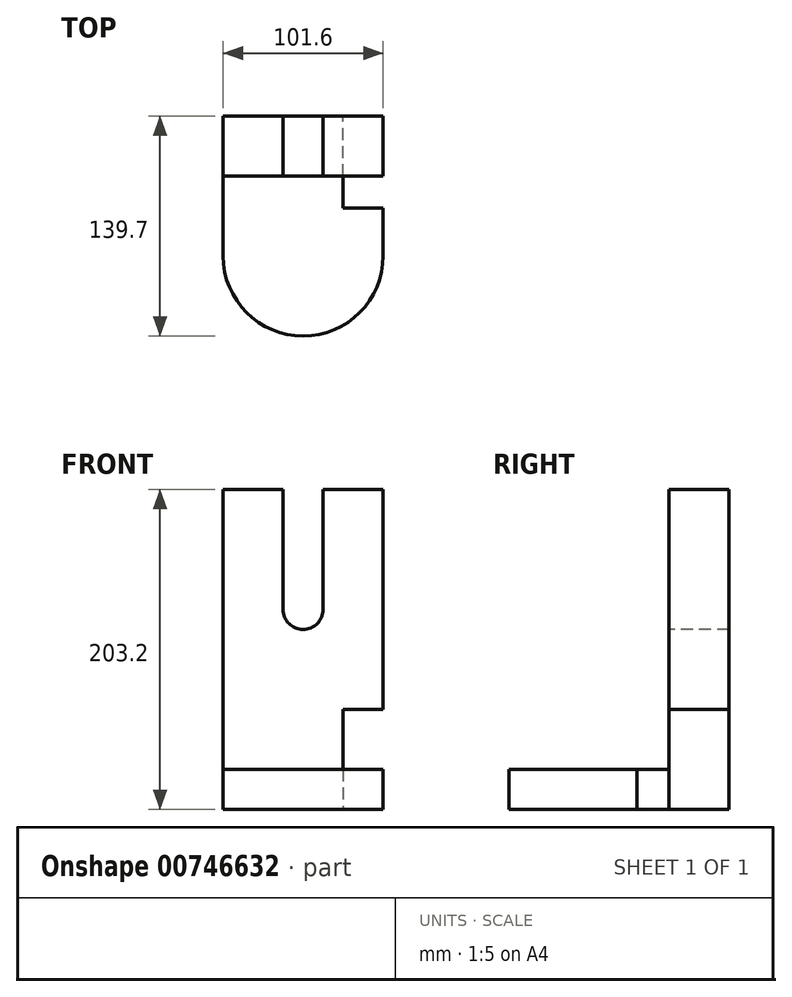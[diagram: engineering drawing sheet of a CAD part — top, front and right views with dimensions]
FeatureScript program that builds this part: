
annotation { "Feature Type Name" : "Feature", "Feature Type Description" : "" }
export const myFeature = defineFeature(function(context is Context, id is Id, definition is map)
    precondition{}
    {
        {
            var Q0;
            Q0=qCreatedBy(makeId("Front.planeOp"),FACE);
            var sketch = newSketch(context, id + "F0", { "sketchPlane" : qUnion([Q0])});
            skLineSegment(sketch, "E0.top", {"start": v(-50.8, -101.6) * mm, "end": v(50.8, -101.6) * mm});
            skLineSegment(sketch, "E0.left", {"start": v(-50.8, 101.6) * mm, "end": v(-50.8, -101.6) * mm});
            skLineSegment(sketch, "E0.right", {"start": v(50.8, 101.6) * mm, "end": v(50.8, -101.6) * mm});
            skLineSegment(sketch, "E1", {"start": v(-50.8, 101.6) * mm, "end": v(50.8, 101.6) * mm});
            skSolve(sketch);
        }
        {
            var Q0;
            Q0=makeQuery(id+"F0.imprint","IMPRINT",FACE,{"disambiguationData":[TD([[makeQuery(id+"F0.imprint","IMPRINT",EDGE,{"derivedFrom":sQuery(id+"F0.wireOp",EDGE,"E0.top")}),1.0]])]});
            extrude(context, id + "F1", {"entities" : qUnion([Q0]), "oppositeDirection" : true, "depth" : 38.1 * mm, "offsetDistance" : 25.4 * mm});
        }
        {
            var Q0;
            Q0=makeQuery(id+"F1.opExtrude","SWEPT_FACE",FACE,{"disambiguationData":[OSD([sQuery(id+"F0.wireOp",EDGE,"E0.top")])]});
            var sketch = newSketch(context, id + "F2", { "sketchPlane" : qUnion([Q0])});
            skLineSegment(sketch, "E2", {"start": v(-50.8, 0) * mm, "end": v(-50.8, 50.8) * mm});
            skLineSegment(sketch, "E3", {"start": v(50.8, 0) * mm, "end": v(50.8, 50.8) * mm});
            skArc(sketch, "E4", {"start": v(50.8, 50.8) * mm, "mid": v(0, 101.6) * mm, "end": v(-50.8, 50.8) * mm});
            skSolve(sketch);
        }
        {
            var Q0;
            Q0=makeQuery(id+"F2.imprint","IMPRINT",FACE,{"disambiguationData":[TD([[makeQuery(id+"F2.imprint","IMPRINT",EDGE,{"derivedFrom":sQuery(id+"F2.wireOp",EDGE,"E2")}),-1.0]])]});
            extrude(context, id + "F3", {"entities" : qUnion([Q0]), "oppositeDirection" : true, "depth" : 25.4 * mm, "offsetDistance" : 25.4 * mm});
        }
        {
            var Q0;
            Q0=makeQuery(id+"F1.opExtrude","CAP_FACE",FACE,{"disambiguationData":[OSD([sQuery(id+"F0.wireOp",EDGE,"E0.top"),sQuery(id+"F0.wireOp",EDGE,"E0.left"),sQuery(id+"F0.wireOp",EDGE,"E0.right"),sQuery(id+"F0.wireOp",EDGE,"E1")])],"isStart":true});
            var sketch = newSketch(context, id + "F4", { "sketchPlane" : qUnion([Q0])});
            skLineSegment(sketch, "E5.bottom", {"start": v(-12.7, 101.6) * mm, "end": v(12.7, 101.6) * mm});
            skLineSegment(sketch, "E5.left", {"start": v(-12.7, 101.6) * mm, "end": v(-12.7, 25.4) * mm});
            skLineSegment(sketch, "E5.right", {"start": v(12.7, 101.6) * mm, "end": v(12.7, 25.4) * mm});
            skArc(sketch, "E6", {"start": v(-12.7, 25.4) * mm, "mid": v(0, 12.7) * mm, "end": v(12.7, 25.4) * mm});
            skSolve(sketch);
        }
        {
            var Q0;
            Q0=makeQuery(id+"F4.imprint","IMPRINT",FACE,{"disambiguationData":[TD([[makeQuery(id+"F4.imprint","IMPRINT",EDGE,{"derivedFrom":sQuery(id+"F4.wireOp",EDGE,"E5.bottom")}),-1.0]])]});
            extrude(context, id + "F5", {"entities" : qUnion([Q0]), "operationType" : NewBodyOperationType.REMOVE, "oppositeDirection" : true, "depth" : 1270 * mm, "offsetDistance" : 25.4 * mm});
        }
        {
            var Q0;
            Q0=makeQuery(id+"F1.opExtrude","SWEPT_FACE",FACE,{"disambiguationData":[OSD([sQuery(id+"F0.wireOp",EDGE,"E0.right")])]});
            var sketch = newSketch(context, id + "F6", { "sketchPlane" : qUnion([Q0])});
            skLineSegment(sketch, "E7.bottom", {"start": v(-20.32, -76.2) * mm, "end": v(0, -76.2) * mm});
            skLineSegment(sketch, "E7.top", {"start": v(-20.32, -101.6) * mm, "end": v(38.1, -101.6) * mm});
            skLineSegment(sketch, "E7.left", {"start": v(-20.32, -76.2) * mm, "end": v(-20.32, -101.6) * mm});
            skLineSegment(sketch, "E7.right", {"start": v(38.1, -76.2) * mm, "end": v(38.1, -101.6) * mm});
            skLineSegment(sketch, "E8.bottom", {"start": v(0, -38.1) * mm, "end": v(38.1, -38.1) * mm});
            skLineSegment(sketch, "E8.top", {"start": v(0, -101.6) * mm, "end": v(38.1, -101.6) * mm});
            skLineSegment(sketch, "E8.left", {"start": v(0, -38.1) * mm, "end": v(0, -76.2) * mm});
            skLineSegment(sketch, "E8.right", {"start": v(38.1, -38.1) * mm, "end": v(38.1, -101.6) * mm});
            skSolve(sketch);
        }
        {
            var Q0;
            {var subQ0=sQuery(id+"F6.wireOp",EDGE,"E7.bottom");Q0=makeQuery(id+"F6.imprint","IMPRINT",FACE,{"disambiguationData":[TD([[makeQuery(id+"F6.imprint","IMPRINT",EDGE,{"derivedFrom":subQ0}),-1.0]])]});}
            var Q1;
            {var subQ2=sQuery(id+"F6.wireOp",EDGE,"E8.bottom");Q1=makeQuery(id+"F6.imprint","IMPRINT",FACE,{"disambiguationData":[TD([[makeQuery(id+"F6.imprint","IMPRINT",EDGE,{"derivedFrom":subQ2}),-1.0]])]});}
            extrude(context, id + "F7", {"entities" : qUnion([Q0, Q1]), "operationType" : NewBodyOperationType.REMOVE, "oppositeDirection" : true, "depth" : 25.4 * mm, "offsetDistance" : 25.4 * mm});
        }
    });
